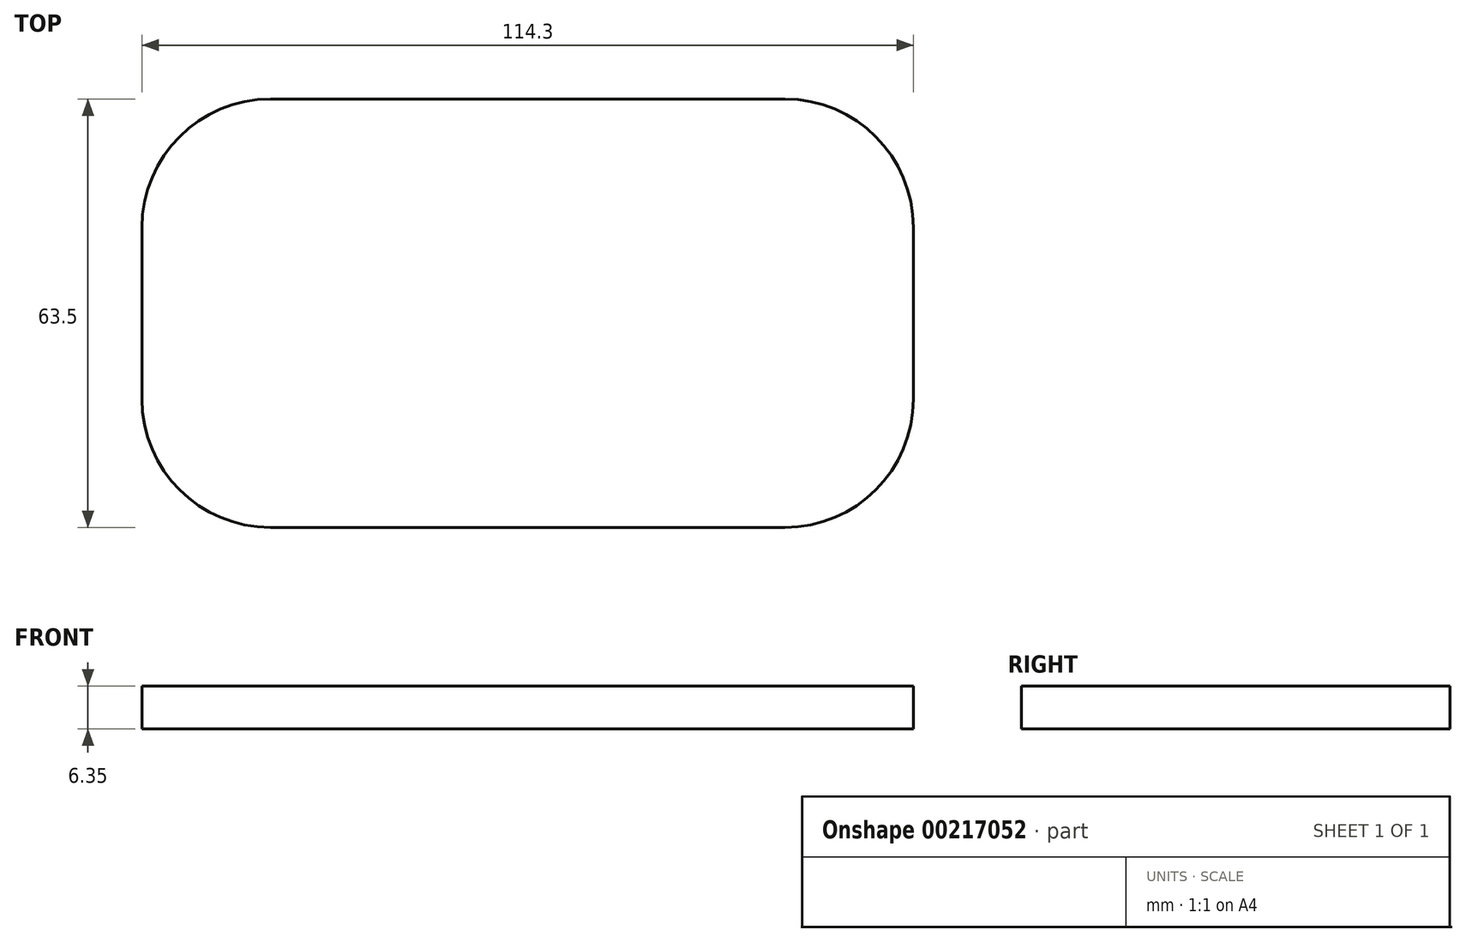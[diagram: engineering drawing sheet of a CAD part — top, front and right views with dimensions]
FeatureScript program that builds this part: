
annotation { "Feature Type Name" : "Feature", "Feature Type Description" : "" }
export const myFeature = defineFeature(function(context is Context, id is Id, definition is map)
    precondition{}
    {
        {
            var Q0;
            Q0=qCreatedBy(makeId("Top.planeOp"),FACE);
            var sketch = newSketch(context, id + "F0", { "sketchPlane" : qUnion([Q0])});
            skArc(sketch, "E0.0", {"start": v(35.97, -34.21) * mm, "mid": v(30.39, -20.74) * mm, "end": v(16.92, -15.16) * mm});
            skLineSegment(sketch, "E0.1", {"start": v(35.97, -59.61) * mm, "end": v(35.97, -34.21) * mm});
            skLineSegment(sketch, "E0.2", {"start": v(16.92, -15.16) * mm, "end": v(-59.28, -15.16) * mm});
            skArc(sketch, "E0.3", {"start": v(16.92, -78.66) * mm, "mid": v(30.39, -73.08) * mm, "end": v(35.97, -59.61) * mm});
            skArc(sketch, "E0.4", {"start": v(-59.28, -15.16) * mm, "mid": v(-72.76, -20.74) * mm, "end": v(-78.33, -34.21) * mm});
            skLineSegment(sketch, "E0.5", {"start": v(-78.33, -59.61) * mm, "end": v(-78.33, -34.21) * mm});
            skArc(sketch, "E0.6", {"start": v(-78.33, -59.61) * mm, "mid": v(-72.76, -73.08) * mm, "end": v(-59.28, -78.66) * mm});
            skLineSegment(sketch, "E0.7", {"start": v(16.92, -78.66) * mm, "end": v(-59.28, -78.66) * mm});
            skSolve(sketch);
        }
        {
            var Q0;
            Q0=makeQuery(id+"F0.imprint","IMPRINT",FACE,{"disambiguationData":[TD([[makeQuery(id+"F0.imprint","IMPRINT",EDGE,{"derivedFrom":sQuery(id+"F0.wireOp",EDGE,"E0.0")}),1.0]])]});
            extrude(context, id + "F1", {"entities" : qUnion([Q0]), "depth" : 6.35 * mm});
        }
    });
